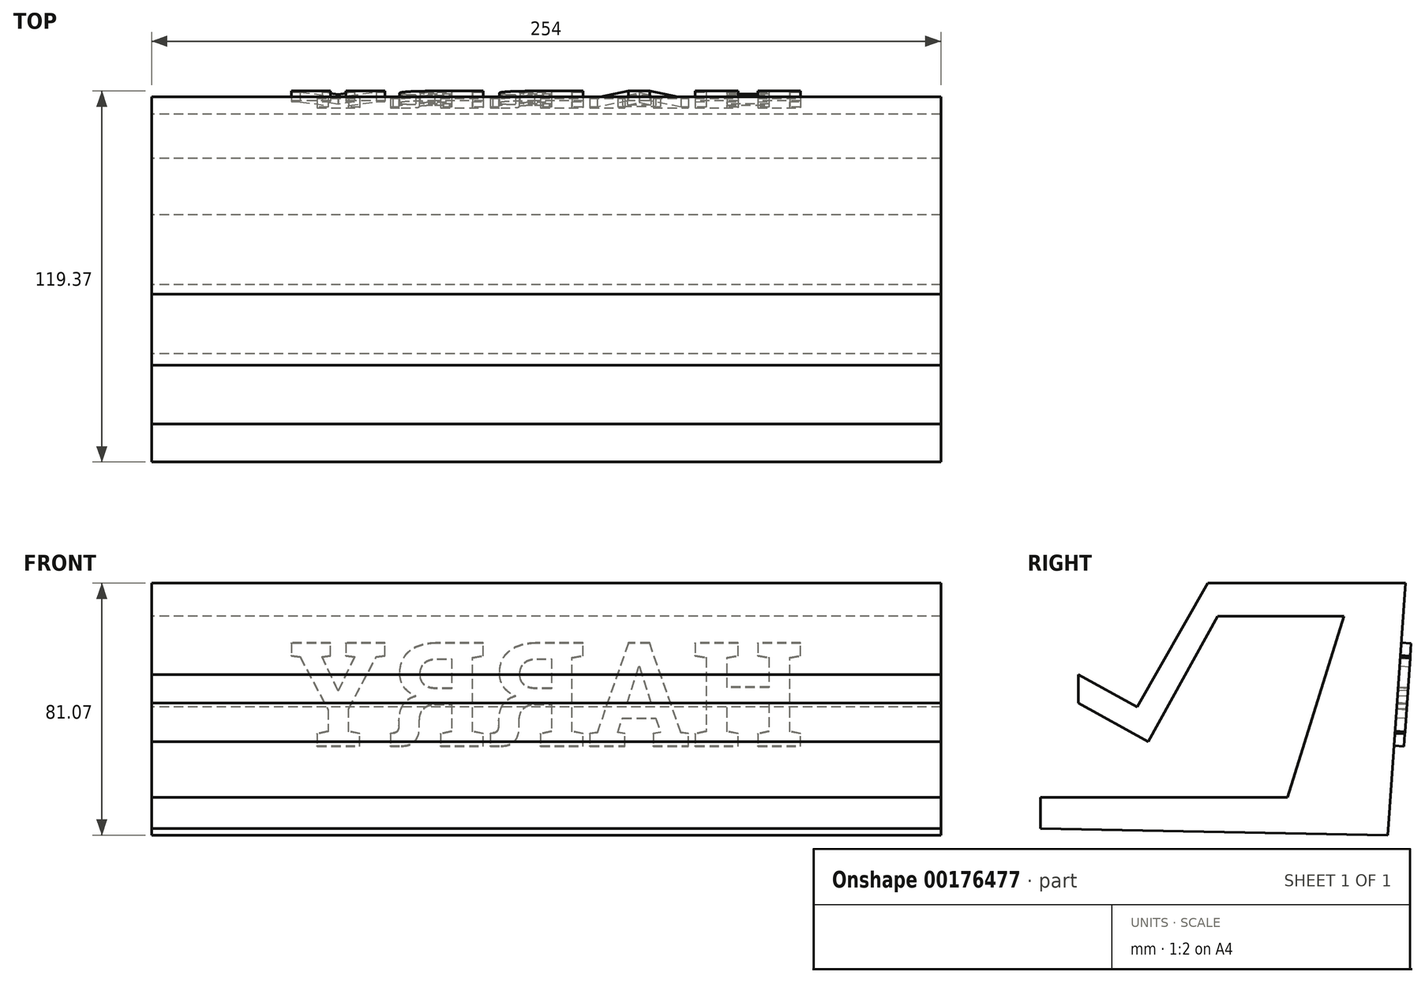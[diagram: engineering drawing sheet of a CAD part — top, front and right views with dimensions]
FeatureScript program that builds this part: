
annotation { "Feature Type Name" : "Feature", "Feature Type Description" : "" }
export const myFeature = defineFeature(function(context is Context, id is Id, definition is map)
    precondition{}
    {
        {
            var Q0;
            Q0=qCreatedBy(makeId("Right.planeOp"),FACE);
            var sketch = newSketch(context, id + "F0", { "sketchPlane" : qUnion([Q0])});
            skLineSegment(sketch, "E0", {"start": v(-36.23, -20.97) * mm, "end": v(-13.99, 19.35) * mm});
            skLineSegment(sketch, "E1", {"start": v(-13.99, 19.35) * mm, "end": v(26.71, 19.35) * mm});
            skLineSegment(sketch, "E2", {"start": v(26.71, 19.35) * mm, "end": v(8.53, -38.86) * mm});
            skLineSegment(sketch, "E3", {"start": v(-39.84, -9.86) * mm, "end": v(-17.07, 30.02) * mm});
            skLineSegment(sketch, "E4", {"start": v(-17.07, 30.02) * mm, "end": v(46.52, 30.02) * mm});
            skLineSegment(sketch, "E5", {"start": v(46.52, 30.02) * mm, "end": v(40.84, -51.05) * mm});
            skLineSegment(sketch, "E6", {"start": v(-39.84, -9.86) * mm, "end": v(-58.76, 0.58) * mm});
            skLineSegment(sketch, "E7", {"start": v(-36.23, -20.97) * mm, "end": v(-58.8, -8.52) * mm});
            skLineSegment(sketch, "E8", {"start": v(-58.8, -8.52) * mm, "end": v(-58.76, 0.58) * mm});
            skLineSegment(sketch, "E9", {"start": v(8.53, -38.86) * mm, "end": v(-71.02, -38.86) * mm});
            skLineSegment(sketch, "E10", {"start": v(-71.02, -38.86) * mm, "end": v(-71.02, -48.92) * mm});
            skLineSegment(sketch, "E11", {"start": v(-71.02, -48.92) * mm, "end": v(40.84, -51.05) * mm});
            skSolve(sketch);
        }
        {
            var Q0;
            Q0=makeQuery(id+"F0.imprint","IMPRINT",FACE,{"disambiguationData":[TD([[makeQuery(id+"F0.imprint","IMPRINT",EDGE,{"derivedFrom":sQuery(id+"F0.wireOp",EDGE,"E0")}),1.0]])]});
            extrude(context, id + "F1", {"entities" : qUnion([Q0]), "depth" : 254 * mm});
        }
        {
            var Q0;
            Q0 = qSketchRegion(id + "F0", true);
            extrude(context, id + "F2", {"entities" : qUnion([Q0]), "operationType" : NewBodyOperationType.ADD, "depth" : 25.4 * mm});
        }
        {
            var Q0;
            Q0=makeQuery(id+"F1.opExtrude","SWEPT_FACE",FACE,{"disambiguationData":[OSD([sQuery(id+"F0.wireOp",EDGE,"E5")])]});
            var sketch = newSketch(context, id + "F3", { "sketchPlane" : qUnion([Q0])});
            skText(sketch, "E12", { "text": "HARRY", "fontName": "RobotoSlab-Bold.ttf"});
            const initialGuessF3  = {"E12": [-0.21018, -0.01923, 1, 0, 0.03361]};
            skSetInitialGuess(sketch, initialGuessF3);
            skSolve(sketch);
        }
        {
            var Q0;
            Q0 = qSketchRegion(id + "F3", true);
            extrude(context, id + "F4", {"entities" : qUnion([Q0]), "operationType" : NewBodyOperationType.ADD, "depth" : 3.17 * mm});
        }
    });
